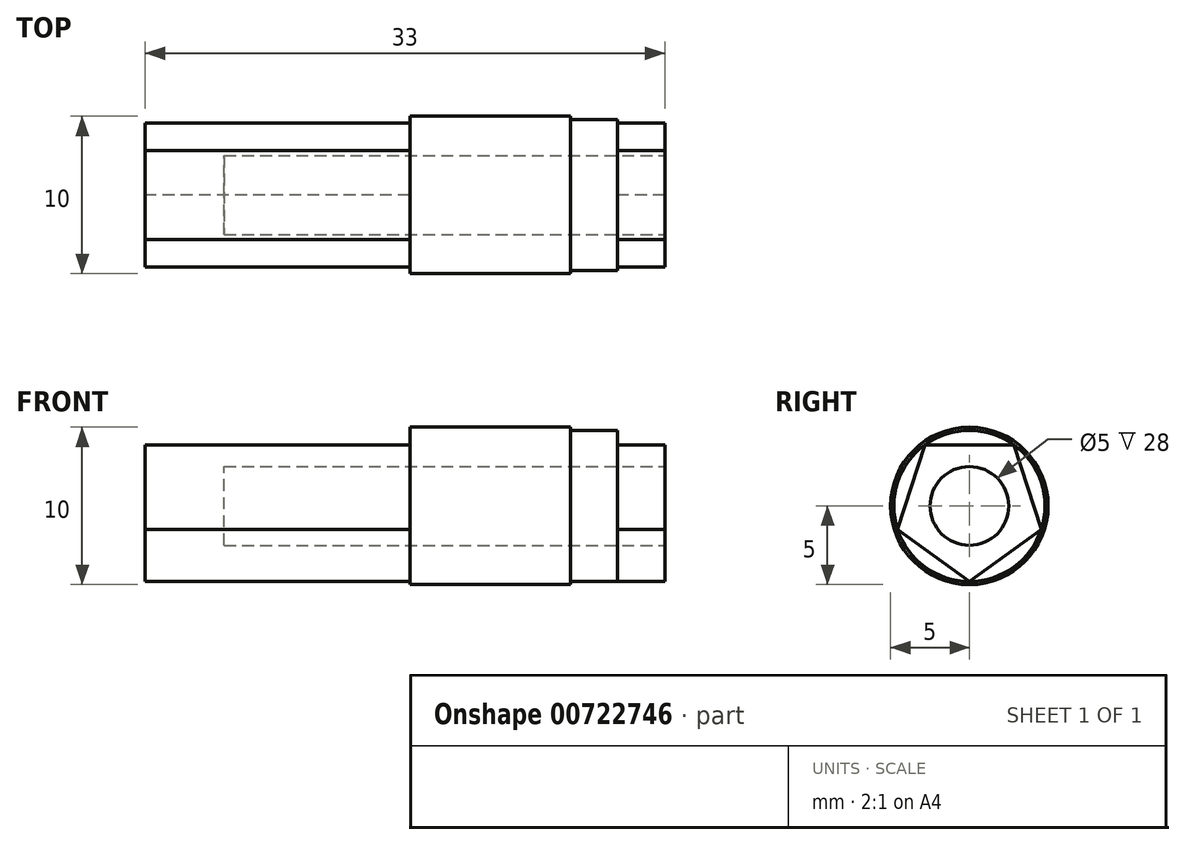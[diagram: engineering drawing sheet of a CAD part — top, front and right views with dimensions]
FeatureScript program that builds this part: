
annotation { "Feature Type Name" : "Feature", "Feature Type Description" : "" }
export const myFeature = defineFeature(function(context is Context, id is Id, definition is map)
    precondition{}
    {
        {
            var Q0;
            Q0=qCreatedBy(makeId("Right.planeOp"),FACE);
            var sketch = newSketch(context, id + "F0", { "sketchPlane" : qUnion([Q0])});
            skCircle(sketch, "E0", {"center": v(0, 0) * mm, "radius": 5 * mm});
            skSolve(sketch);
        }
        {
            var Q0;
            Q0=qSketchRegion(id+"F0",true);
            extrude(context, id + "F1", {"entities" : qUnion([Q0]), "oppositeDirection" : true, "depth" : 10.2 * mm, "offsetDistance" : 25 * mm});
        }
        {
            var Q0;
            Q0=makeQuery(id+"F1.opExtrude","CAP_FACE",FACE,{"disambiguationData":[OSD([sQuery(id+"F0.wireOp",EDGE,"E0")])],"isStart":true});
            var sketch = newSketch(context, id + "F2", { "sketchPlane" : qUnion([Q0])});
            skCircle(sketch, "E1", {"center": v(0, 0) * mm, "radius": 4.8 * mm});
            skSolve(sketch);
        }
        {
            var Q0;
            Q0=qSketchRegion(id+"F2",true);
            extrude(context, id + "F3", {"entities" : qUnion([Q0]), "operationType" : NewBodyOperationType.ADD, "depth" : 3 * mm, "offsetDistance" : 25 * mm});
        }
        {
            var Q0;
            Q0=makeQuery(id+"F3.opExtrude","CAP_FACE",FACE,{"disambiguationData":[OSD([sQuery(id+"F2.wireOp",EDGE,"E1")])],"isStart":false});
            var sketch = newSketch(context, id + "F4", { "sketchPlane" : qUnion([Q0])});
            skCircle(sketch, "E2.cCircle", {"center": v(0, 0) * mm, "radius": 4.8 * mm, "construction": true});
            skLineSegment(sketch, "E2.0", {"start": v(0, -4.8) * mm, "end": v(-4.57, -1.48) * mm});
            skLineSegment(sketch, "E2.1", {"start": v(-4.57, -1.48) * mm, "end": v(-2.82, 3.88) * mm});
            skLineSegment(sketch, "E2.2", {"start": v(-2.82, 3.88) * mm, "end": v(2.82, 3.88) * mm});
            skLineSegment(sketch, "E2.3", {"start": v(2.82, 3.88) * mm, "end": v(4.57, -1.48) * mm});
            skLineSegment(sketch, "E2.4", {"start": v(4.57, -1.48) * mm, "end": v(0, -4.8) * mm});
            skSolve(sketch);
        }
        {
            var Q0;
            Q0=qSketchRegion(id+"F4",true);
            extrude(context, id + "F5", {"entities" : qUnion([Q0]), "operationType" : NewBodyOperationType.ADD, "depth" : 3 * mm, "offsetDistance" : 25 * mm, "hasSecondDirection" : true, "secondDirectionOppositeDirection" : true, "secondDirectionDepth" : 30 * mm});
        }
        {
            var Q0;
            Q0=makeQuery(id+"F5.opExtrude","CAP_FACE",FACE,{"disambiguationData":[OSD([sQuery(id+"F4.wireOp",EDGE,"E2.0"),sQuery(id+"F4.wireOp",EDGE,"E2.1"),sQuery(id+"F4.wireOp",EDGE,"E2.2"),sQuery(id+"F4.wireOp",EDGE,"E2.3"),sQuery(id+"F4.wireOp",EDGE,"E2.4")])],"isStart":false});
            var sketch = newSketch(context, id + "F6", { "sketchPlane" : qUnion([Q0])});
            skCircle(sketch, "E3", {"center": v(0, 0) * mm, "radius": 2.5 * mm});
            skSolve(sketch);
        }
        {
            var Q0;
            Q0=qSketchRegion(id+"F6",true);
            extrude(context, id + "F7", {"entities" : qUnion([Q0]), "operationType" : NewBodyOperationType.REMOVE, "oppositeDirection" : true, "depth" : 28 * mm, "offsetDistance" : 25 * mm});
        }
    });
